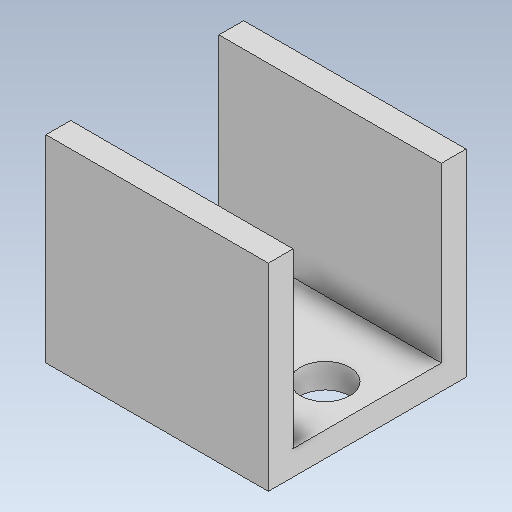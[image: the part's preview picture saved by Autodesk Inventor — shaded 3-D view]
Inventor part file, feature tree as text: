
AUTODESK INVENTOR PART (.ipt)
format: ipt  version: 2021 (Build 250183000, 183)  size: 109,568 bytes
history: native  units: in
note: dims shown in document units (in); Inventor stores cm internally (conversion verified against a paired STEP export)
features: other x3, sketch x1
ambient origin geometry x8: Origin, YZ Plane, XZ Plane, XY Plane, X Axis, Y Axis, Z Axis, Center Point
bodies: Solid1 (feature_tree)
feature tree (4):
  other  "halfinchCChannel.ipt"
  other  "Solid1::halfinchCChannel.ipt"
  other  "TaggingFeature1"
  sketch  "Sketch2"  dims[d0=0.3937in]
